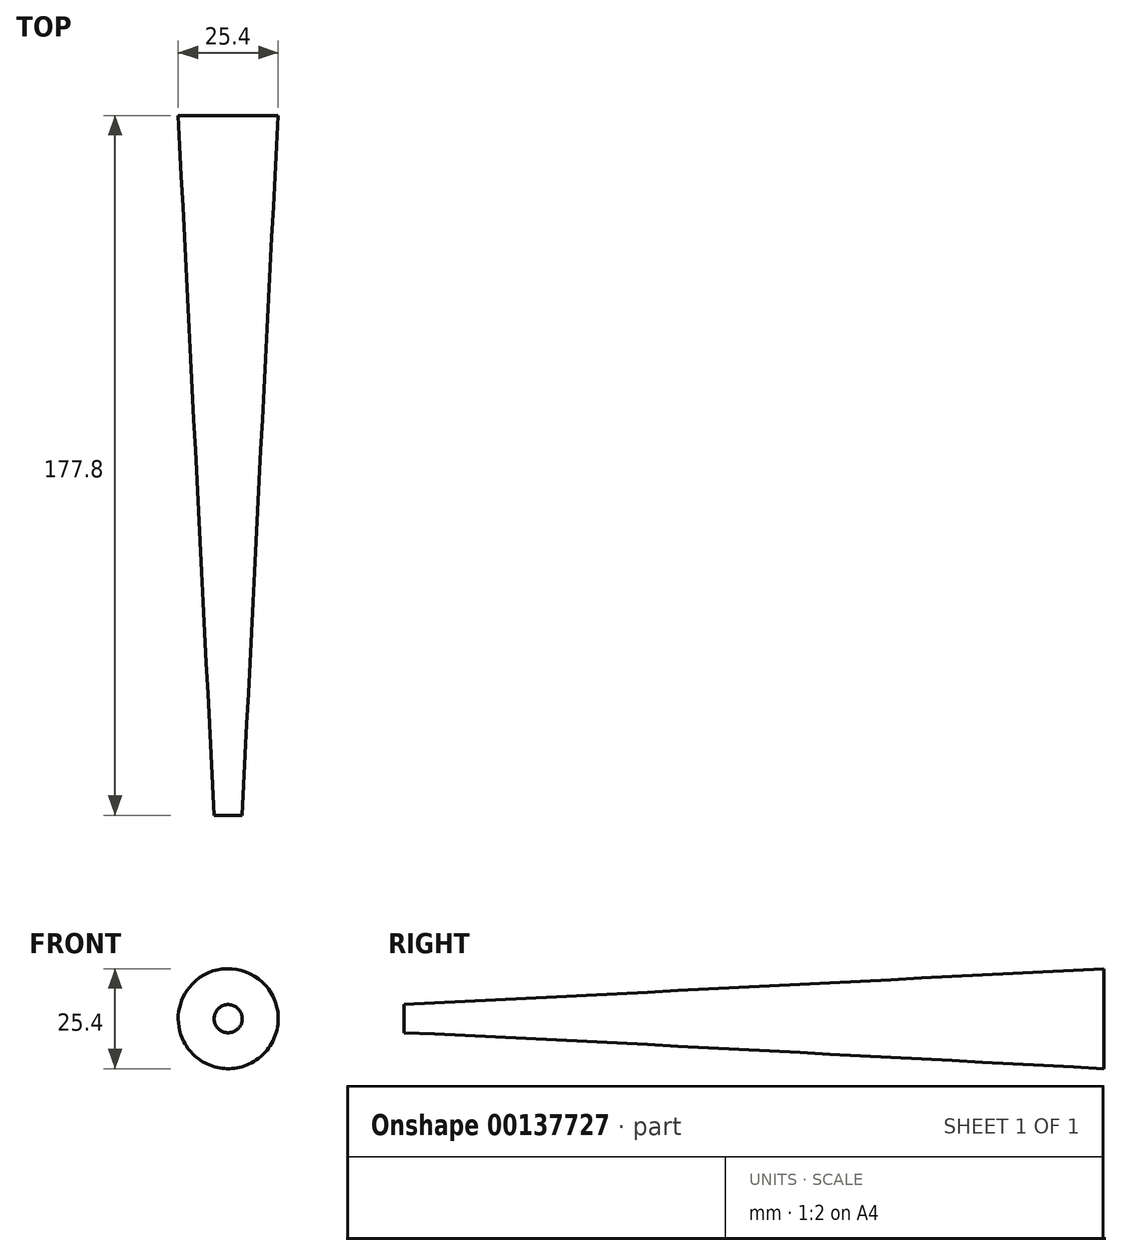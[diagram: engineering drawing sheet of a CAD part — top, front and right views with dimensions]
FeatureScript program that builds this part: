
annotation { "Feature Type Name" : "Feature", "Feature Type Description" : "" }
export const myFeature = defineFeature(function(context is Context, id is Id, definition is map)
    precondition{}
    {
        {
            var Q0;
            Q0=qCreatedBy(makeId("Front.planeOp"),FACE);
            var sketch = newSketch(context, id + "F0", { "sketchPlane" : qUnion([Q0])});
            skArc(sketch, "E0", {"start": v(-9.2, 8.76) * mm, "mid": v(-12.57, 1.8) * mm, "end": v(-11.29, -5.82) * mm});
            skArc(sketch, "E1", {"start": v(8.73, 9.22) * mm, "mid": v(-0.33, 12.7) * mm, "end": v(-9.2, 8.76) * mm});
            skArc(sketch, "E2", {"start": v(6.52, -10.9) * mm, "mid": v(12.62, -1.39) * mm, "end": v(8.73, 9.22) * mm});
            skArc(sketch, "E3", {"start": v(-11.29, -5.82) * mm, "mid": v(-3.48, -12.21) * mm, "end": v(6.52, -10.9) * mm});
            skSolve(sketch);
        }
        {
            var Q0;
            Q0=qCreatedBy(makeId("Front.planeOp"),FACE);
            cPlane(context, id + "F1", {"entities" : qUnion([Q0]), "cplaneType" : CPlaneType.OFFSET, "offset" : 177.8 * mm, "width" : 152.4 * mm, "height" : 152.4 * mm});
        }
        {
            var Q0;
            Q0=qCreatedBy(id+"F1.planeOp",FACE);
            var sketch = newSketch(context, id + "F2", { "sketchPlane" : qUnion([Q0])});
            skArc(sketch, "E4", {"start": v(2.75, 2.28) * mm, "mid": v(0.43, 3.55) * mm, "end": v(-2.12, 2.88) * mm});
            skArc(sketch, "E5", {"start": v(-0.01, -3.58) * mm, "mid": v(3.23, -1.53) * mm, "end": v(2.75, 2.28) * mm});
            skArc(sketch, "E6", {"start": v(-2.12, 2.88) * mm, "mid": v(-3.44, 0.96) * mm, "end": v(-3.3, -1.36) * mm});
            skArc(sketch, "E7", {"start": v(-3.3, -1.36) * mm, "mid": v(-2, -2.97) * mm, "end": v(-0.01, -3.58) * mm});
            skSolve(sketch);
        }
        {
            var Q0;
            Q0 = qSketchRegion(id + "F0", true);
            var Q1;
            Q1 = qSketchRegion(id + "F2", true);
            loft(context, id + "F3", {"sheetProfilesArray" : [{ "sheetProfileEntities" : qUnion([Q0]) }, { "sheetProfileEntities" : qUnion([Q1]) }]});
        }
    });
